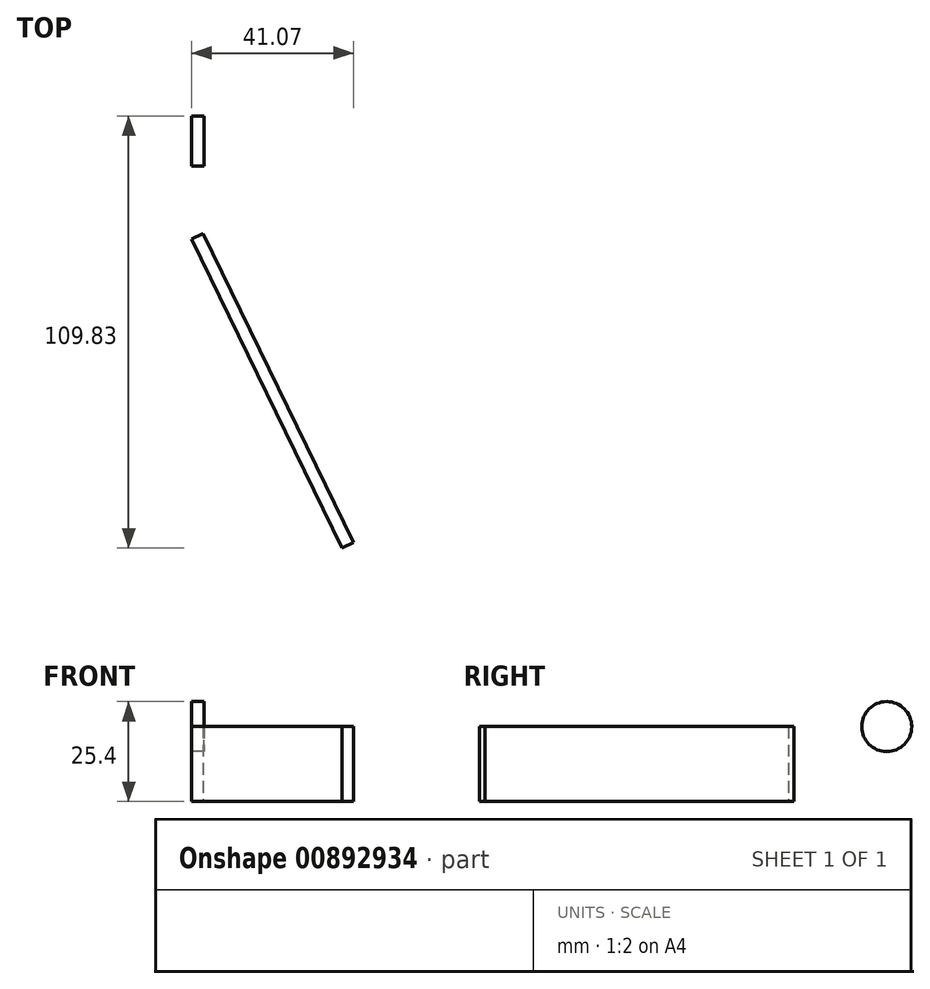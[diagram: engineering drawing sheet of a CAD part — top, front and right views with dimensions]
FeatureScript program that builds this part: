
annotation { "Feature Type Name" : "Feature", "Feature Type Description" : "" }
export const myFeature = defineFeature(function(context is Context, id is Id, definition is map)
    precondition{}
    {
        {
            var Q0;
            Q0=qCreatedBy(makeId("Top.planeOp"),FACE);
            var sketch = newSketch(context, id + "F0", { "sketchPlane" : qUnion([Q0])});
            skLineSegment(sketch, "E0", {"start": v(517.13, -39.69) * mm, "end": v(517.13, -1004.89) * mm, "construction": true});
            skLineSegment(sketch, "E1", {"start": v(517.13, -1004.89) * mm, "end": v(428.23, -1004.89) * mm, "construction": true});
            skLineSegment(sketch, "E2", {"start": v(-16.41, -90.75) * mm, "end": v(428.23, -1004.89) * mm, "construction": true});
            skLineSegment(sketch, "E3", {"start": v(-41.28, -39.69) * mm, "end": v(-41.28, 0) * mm});
            skCircle(sketch, "E4", {"center": v(-0.15, -66.28) * mm, "radius": 22.23 * mm});
            skLineSegment(sketch, "E5.0", {"start": v(517.13, 0) * mm, "end": v(-41.28, 0) * mm});
            skLineSegment(sketch, "E6", {"start": v(-41.28, -39.69) * mm, "end": v(-16.41, -90.75) * mm});
            skLineSegment(sketch, "E7", {"start": v(-41.28, -39.69) * mm, "end": v(448.4, -39.69) * mm});
            skLineSegment(sketch, "E8", {"start": v(517.13, 0) * mm, "end": v(517.13, -39.69) * mm});
            skLineSegment(sketch, "E9", {"start": v(-16.41, -90.75) * mm, "end": v(412.08, -60.66) * mm});
            skCircle(sketch, "E10", {"center": v(-0.15, -66.28) * mm, "radius": 6.35 * mm});
            skLineSegment(sketch, "E11", {"start": v(517.13, 0) * mm, "end": v(412.08, -60.66) * mm});
            skLineSegment(sketch, "E12", {"start": v(0, -8.41) * mm, "end": v(38.22, -86.91) * mm});
            skLineSegment(sketch, "E13", {"start": v(0, -8.41) * mm, "end": v(0, 0) * mm});
            skSolve(sketch);
        }
        {
            var Q0;
            Q0=qCreatedBy(makeId("Right.planeOp"),FACE);
            var sketch = newSketch(context, id + "F1", { "sketchPlane" : qUnion([Q0])});
            skLineSegment(sketch, "E14.MirrorCS", {"start": v(-6.54, 62.3) * mm, "end": v(0.74, 64.25) * mm});
            skLineSegment(sketch, "E15.MirrorCS", {"start": v(0.74, 64.25) * mm, "end": v(-7.96, 61.91) * mm});
            skLineSegment(sketch, "E16.MirrorCS", {"start": v(42.54, 75.45) * mm, "end": v(29.11, 71.85) * mm});
            skLineSegment(sketch, "E17.MirrorCS", {"start": v(36.4, 73.8) * mm, "end": v(29.11, 71.85) * mm, "construction": true});
            skCircle(sketch, "E18.MirrorC", {"center": v(16.57, 61.91) * mm, "radius": 6.35 * mm});
            skCircle(sketch, "E19.MirrorC", {"center": v(16.57, 61.91) * mm, "radius": 9.53 * mm, "construction": true});
            skLineSegment(sketch, "E20.MirrorCS", {"start": v(29.11, 71.85) * mm, "end": v(42.54, 75.45) * mm, "construction": true});
            skLineSegment(sketch, "E21.MirrorCS", {"start": v(42.54, 75.45) * mm, "end": v(49.12, 50.91) * mm});
            skLineSegment(sketch, "E22.MirrorCS", {"start": v(-39.69, 61.91) * mm, "end": v(-6.44, 61.91) * mm});
            skLineSegment(sketch, "E23.MirrorCS", {"start": v(23.25, 122.87) * mm, "end": v(-19.69, 111.36) * mm, "construction": true});
            skLineSegment(sketch, "E24.MirrorCS", {"start": v(1.78, 117.12) * mm, "end": v(-7.42, 114.65) * mm});
            skLineSegment(sketch, "E25.MirrorCS", {"start": v(-33.72, 212.79) * mm, "end": v(-15.32, 217.72) * mm});
            skArc(sketch, "E26.MirrorCS", {"start": v(0.62, 64.21) * mm, "mid": v(12.4, 77.48) * mm, "end": v(29.23, 71.88) * mm});
            skArc(sketch, "E27.MirrorCS", {"start": v(36.4, 73.8) * mm, "mid": v(20.68, 46.58) * mm, "end": v(-6.54, 62.3) * mm, "construction": true});
            skLineSegment(sketch, "E28.MirrorCS", {"start": v(-19.69, 111.36) * mm, "end": v(-6.54, 62.3) * mm, "construction": true});
            skLineSegment(sketch, "E29.MirrorCS", {"start": v(-15.32, 217.72) * mm, "end": v(10.98, 119.58) * mm, "construction": true});
            skLineSegment(sketch, "E30.MirrorCS", {"start": v(-39.69, 61.91) * mm, "end": v(-39.69, 0) * mm});
            skLineSegment(sketch, "E31.MirrorCS", {"start": v(23.25, 122.87) * mm, "end": v(36.4, 73.8) * mm, "construction": true});
            skLineSegment(sketch, "E32.MirrorCS", {"start": v(-7.42, 114.65) * mm, "end": v(-33.72, 212.79) * mm, "construction": true});
            skPoint(sketch, "E33.MirrorP", {"position": v(0, -39.69) * mm});
            skPoint(sketch, "E34.MirrorP", {"position": v(39.69, 0) * mm});
            skCircle(sketch, "E35.MirrorC", {"center": v(0, 0) * mm, "radius": 39.69 * mm});
            skPoint(sketch, "E36.MirrorP", {"position": v(-39.69, 61.91) * mm});
            skPoint(sketch, "E37.MirrorP", {"position": v(39.69, 61.91) * mm});
            skLineSegment(sketch, "E38.MirrorCS", {"start": v(49.12, 50.91) * mm, "end": v(39.69, 0) * mm});
            skLineSegment(sketch, "E39", {"start": v(0, 39.69) * mm, "end": v(-39.69, 39.69) * mm});
            skLineSegment(sketch, "E40", {"start": v(0, 39.69) * mm, "end": v(0, 42.86) * mm});
            skLineSegment(sketch, "E41", {"start": v(0, 42.86) * mm, "end": v(-39.69, 42.86) * mm});
            skPoint(sketch, "E42.0", {"position": v(-8.41, 0) * mm});
            skLineSegment(sketch, "E43.trimOffspring", {"start": v(-8.41, 42.86) * mm, "end": v(-8.41, 61.91) * mm});
            skSolve(sketch);
        }
        {
            var Q0;
            Q0=sQuery(id+"F0.wireOp",EDGE,"E12");
            cPlane(context, id + "F2", {"entities" : qUnion([Q0]), "cplaneType" : CPlaneType.LINE_ANGLE, "offset" : 25.4 * mm, "angle" : 90 * degree, "oppositeDirection" : true, "width" : 152.4 * mm, "height" : 152.4 * mm});
        }
        {
            var Q0;
            Q0=qCreatedBy(id+"F2.planeOp",FACE);
            var sketch = newSketch(context, id + "F3", { "sketchPlane" : qUnion([Q0])});
            skPoint(sketch, "E44.0", {"position": v(7.56, 42.86) * mm});
            skLineSegment(sketch, "E45.0", {"start": v(7.56, 42.86) * mm, "end": v(94.87, 42.86) * mm});
            skLineSegment(sketch, "E46", {"start": v(7.56, 42.86) * mm, "end": v(7.56, 39.69) * mm});
            skLineSegment(sketch, "E47", {"start": v(7.56, 39.69) * mm, "end": v(94.87, 39.69) * mm});
            skPoint(sketch, "E48.0", {"position": v(7.56, 61.91) * mm});
            skLineSegment(sketch, "E49", {"start": v(7.56, 61.91) * mm, "end": v(94.87, 61.91) * mm});
            skPoint(sketch, "E50.0", {"position": v(94.87, 0) * mm});
            skLineSegment(sketch, "E51", {"start": v(94.87, 39.69) * mm, "end": v(94.87, 61.91) * mm});
            skLineSegment(sketch, "E52", {"start": v(7.56, 61.91) * mm, "end": v(7.56, 42.86) * mm});
            skSolve(sketch);
        }
        {
            var Q0;
            Q0=makeQuery(id+"F1.imprint","IMPRINT",FACE,{"disambiguationData":[TD([[makeQuery(id+"F1.imprint","IMPRINT",EDGE,{"derivedFrom":sQuery(id+"F1.wireOp",EDGE,"E18.MirrorC")}),1.0]])]});
            extrude(context, id + "F4", {"entities" : qUnion([Q0]), "depth" : 3.17 * mm, "offsetDistance" : 25.4 * mm});
        }
        {
            var Q0;
            {var subQ0=sQuery(id+"F3.wireOp",EDGE,"E45.0");Q0=makeQuery(id+"F3.imprint","IMPRINT",FACE,{"disambiguationData":[TD([[makeQuery(id+"F3.imprint","IMPRINT",EDGE,{"derivedFrom":subQ0}),1.0]])]});}
            extrude(context, id + "F5", {"entities" : qUnion([Q0]), "oppositeDirection" : true, "depth" : 3.17 * mm, "offsetDistance" : 25.4 * mm});
        }
    });
